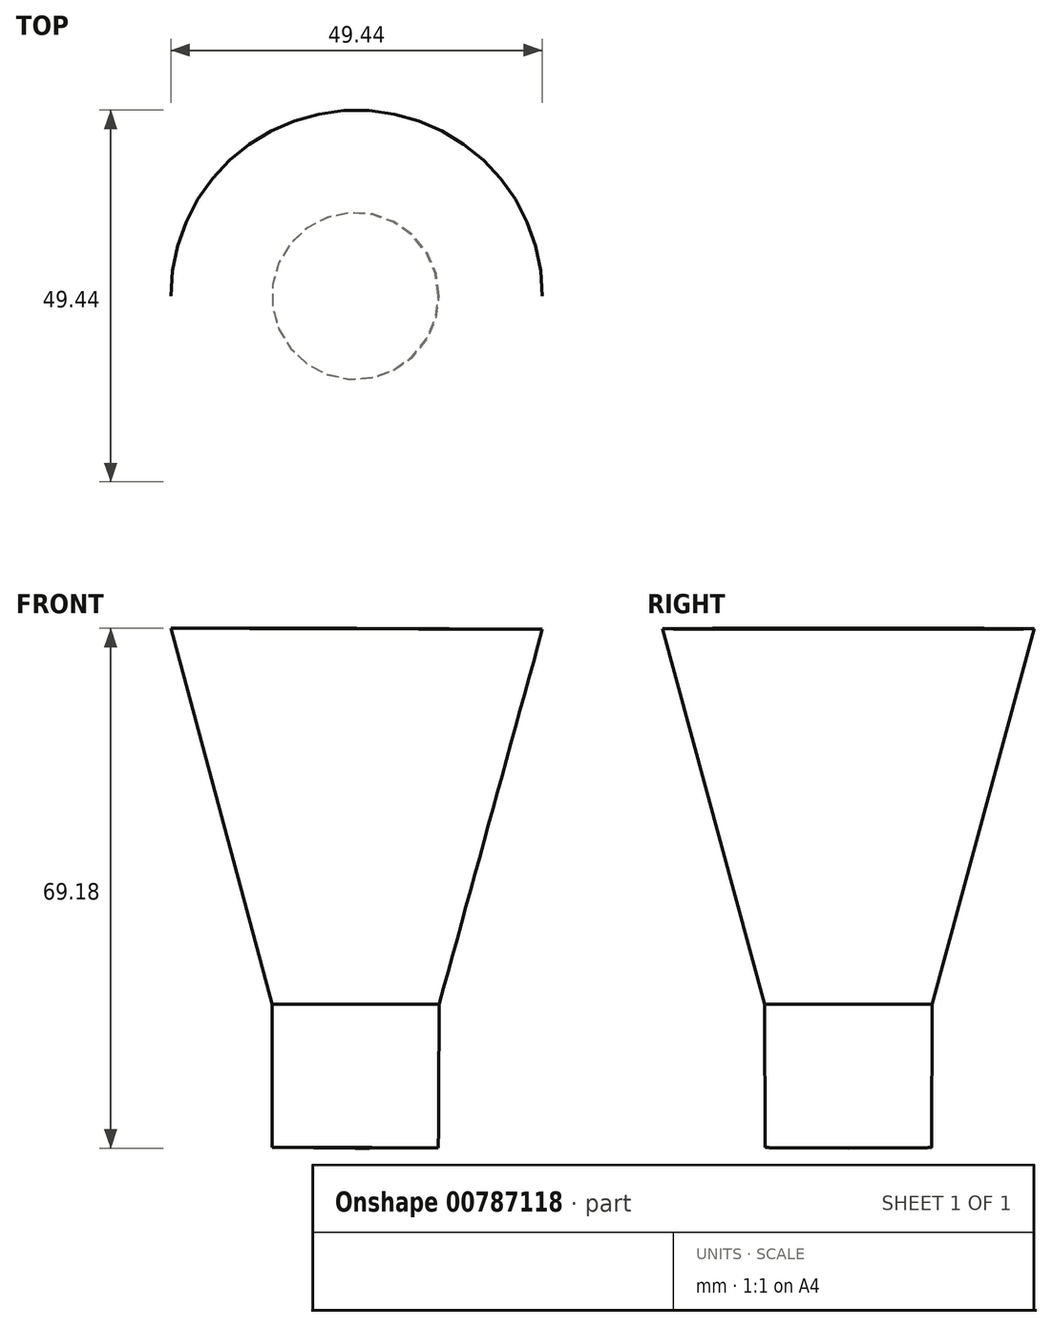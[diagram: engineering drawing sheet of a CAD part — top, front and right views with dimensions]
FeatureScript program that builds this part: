
annotation { "Feature Type Name" : "Feature", "Feature Type Description" : "" }
export const myFeature = defineFeature(function(context is Context, id is Id, definition is map)
    precondition{}
    {
        {
            var Q0;
            Q0=qCreatedBy(makeId("Front.planeOp"),FACE);
            var sketch = newSketch(context, id + "F0", { "sketchPlane" : qUnion([Q0])});
            skLineSegment(sketch, "E0", {"start": v(-11.25, -17.3) * mm, "end": v(10.89, -17.3) * mm});
            skLineSegment(sketch, "E1", {"start": v(-11.25, -17.3) * mm, "end": v(-24.72, 32.7) * mm});
            skLineSegment(sketch, "E2", {"start": v(-24.72, 32.7) * mm, "end": v(24.72, 32.7) * mm});
            skLineSegment(sketch, "E3", {"start": v(24.72, 32.7) * mm, "end": v(10.89, -17.3) * mm});
            skLineSegment(sketch, "E4", {"start": v(-11.25, -17.3) * mm, "end": v(-11.25, -36.38) * mm});
            skLineSegment(sketch, "E5", {"start": v(10.89, -17.3) * mm, "end": v(10.89, -36.6) * mm});
            skLineSegment(sketch, "E6", {"start": v(-11.25, -36.38) * mm, "end": v(10.89, -36.6) * mm});
            skPoint(sketch, "E7.endSnap0", {"position": v(-0.18, -36.5) * mm});
            skPoint(sketch, "E8", {"position": v(0, 0) * mm});
            skLineSegment(sketch, "E9", {"start": v(0, 32.7) * mm, "end": v(-0.18, -36.5) * mm});
            skSolve(sketch);
        }
        {
            var Q0;
            {var subQ0=sQuery(id+"F0.wireOp",EDGE,"E1");Q0=makeQuery(id+"F0.imprint","IMPRINT",FACE,{"disambiguationData":[TD([[makeQuery(id+"F0.imprint","IMPRINT",EDGE,{"derivedFrom":subQ0}),-1.0]])]});}
            var Q1;
            {var subQ0=sQuery(id+"F0.wireOp",EDGE,"E4");Q1=makeQuery(id+"F0.imprint","IMPRINT",FACE,{"disambiguationData":[TD([[makeQuery(id+"F0.imprint","IMPRINT",EDGE,{"derivedFrom":subQ0}),1.0]])]});}
            var Q2;
            Q2=sQuery(id+"F0.wireOp",EDGE,"E9");
            revolve(context, id + "F1", {"surfaceOperationType" : NewSurfaceOperationType.NEW, "entities" : qUnion([Q0, Q1]), "axis" : qUnion([Q2]), "revolveType" : RevolveType.FULL});
        }
    });
